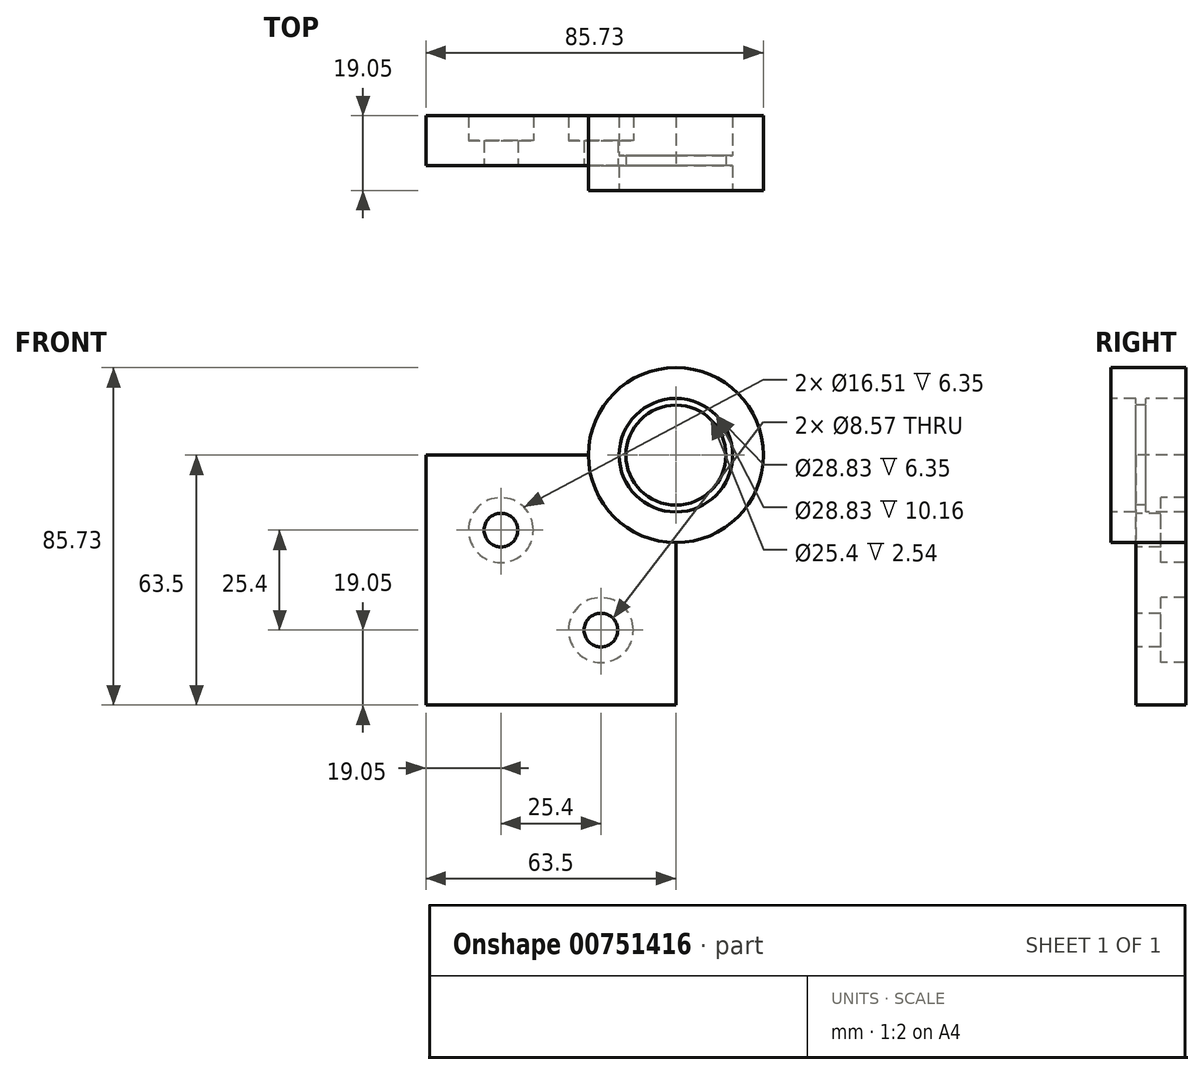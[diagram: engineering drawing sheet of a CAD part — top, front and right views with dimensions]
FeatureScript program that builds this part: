
annotation { "Feature Type Name" : "Feature", "Feature Type Description" : "" }
export const myFeature = defineFeature(function(context is Context, id is Id, definition is map)
    precondition{}
    {
        {
            var Q0;
            Q0=qCreatedBy(makeId("Front.planeOp"),FACE);
            var sketch = newSketch(context, id + "F0", { "sketchPlane" : qUnion([Q0])});
            skCircle(sketch, "E0", {"center": v(0, 0) * mm, "radius": 14.41 * mm});
            skCircle(sketch, "E1", {"center": v(0, 0) * mm, "radius": 12.7 * mm});
            skCircle(sketch, "E2", {"center": v(0, 0) * mm, "radius": 22.23 * mm});
            skLineSegment(sketch, "E3.bottom", {"start": v(0, 0) * mm, "end": v(-63.5, 0) * mm});
            skLineSegment(sketch, "E3.top", {"start": v(0, -63.5) * mm, "end": v(-63.5, -63.5) * mm});
            skLineSegment(sketch, "E3.left", {"start": v(0, 0) * mm, "end": v(0, -63.5) * mm});
            skLineSegment(sketch, "E3.right", {"start": v(-63.5, 0) * mm, "end": v(-63.5, -63.5) * mm});
            skCircle(sketch, "E4", {"center": v(-44.45, -19.05) * mm, "radius": 4.29 * mm});
            skCircle(sketch, "E5", {"center": v(-19.05, -44.45) * mm, "radius": 4.29 * mm});
            skCircle(sketch, "E6", {"center": v(-44.45, -19.05) * mm, "radius": 8.26 * mm});
            skCircle(sketch, "E7", {"center": v(-19.05, -44.45) * mm, "radius": 8.26 * mm});
            skSolve(sketch);
        }
        {
            var Q0;
            {var subQ0=sQuery(id+"F0.wireOp",EDGE,"E3.top");Q0=makeQuery(id+"F0.imprint","IMPRINT",FACE,{"disambiguationData":[TD([[makeQuery(id+"F0.imprint","IMPRINT",EDGE,{"derivedFrom":subQ0}),-1.0]])]});}
            extrude(context, id + "F1", {"entities" : qUnion([Q0]), "depth" : 12.7 * mm, "offsetDistance" : 25.4 * mm});
        }
        {
            var Q0;
            Q0=makeQuery(id+"F0.imprint","IMPRINT",FACE,{"disambiguationData":[TD([[makeQuery(id+"F0.imprint","IMPRINT",EDGE,{"derivedFrom":sQuery(id+"F0.wireOp",EDGE,"E4")}),-1.0]])]});
            var Q1;
            Q1=makeQuery(id+"F0.imprint","IMPRINT",FACE,{"disambiguationData":[TD([[makeQuery(id+"F0.imprint","IMPRINT",EDGE,{"derivedFrom":sQuery(id+"F0.wireOp",EDGE,"E5")}),-1.0]])]});
            extrude(context, id + "F2", {"entities" : qUnion([Q0, Q1]), "operationType" : NewBodyOperationType.ADD, "depth" : 6.35 * mm, "offsetDistance" : 25.4 * mm});
        }
        {
            var Q0;
            {var subQ0=sQuery(id+"F0.wireOp",EDGE,"E3.bottom");var subQ1=sQuery(id+"F0.wireOp",EDGE,"E0");var subQ2=makeQuery(id+"F0.imprint","INTERSECT",VERTEX,{"derivedFrom":[subQ1,subQ0]});Q0=makeQuery(id+"F0.imprint","IMPRINT",FACE,{"disambiguationData":[TD([[makeQuery(id+"F0.imprint","IMPRINT",EDGE,{"disambiguationData":[TD([[subQ2,-1.0]])],"derivedFrom":subQ1}),-1.0]])]});}
            var Q1;
            {var subQ0=sQuery(id+"F0.wireOp",EDGE,"E3.bottom");var subQ1=sQuery(id+"F0.wireOp",EDGE,"E0");var subQ2=makeQuery(id+"F0.imprint","INTERSECT",VERTEX,{"derivedFrom":[subQ1,subQ0]});Q1=makeQuery(id+"F0.imprint","IMPRINT",FACE,{"disambiguationData":[TD([[makeQuery(id+"F0.imprint","IMPRINT",EDGE,{"disambiguationData":[TD([[subQ2,1.0]])],"derivedFrom":subQ1}),-1.0]])]});}
            extrude(context, id + "F3", {"entities" : qUnion([Q0, Q1]), "operationType" : NewBodyOperationType.ADD, "depth" : 12.7 * mm, "offsetDistance" : 25.4 * mm, "hasSecondDirection" : true, "secondDirectionOppositeDirection" : true, "secondDirectionDepth" : 6.35 * mm});
        }
        {
            var Q0;
            {var subQ0=sQuery(id+"F0.wireOp",EDGE,"E3.bottom");var subQ1=sQuery(id+"F0.wireOp",EDGE,"E0");var subQ2=makeQuery(id+"F0.imprint","INTERSECT",VERTEX,{"derivedFrom":[subQ1,subQ0]});Q0=makeQuery(id+"F0.imprint","IMPRINT",FACE,{"disambiguationData":[TD([[makeQuery(id+"F0.imprint","IMPRINT",EDGE,{"disambiguationData":[TD([[subQ2,-1.0]])],"derivedFrom":subQ1}),1.0]])]});}
            var Q1;
            {var subQ0=sQuery(id+"F0.wireOp",EDGE,"E3.bottom");var subQ1=sQuery(id+"F0.wireOp",EDGE,"E0");var subQ2=makeQuery(id+"F0.imprint","INTERSECT",VERTEX,{"derivedFrom":[subQ1,subQ0]});Q1=makeQuery(id+"F0.imprint","IMPRINT",FACE,{"disambiguationData":[TD([[makeQuery(id+"F0.imprint","IMPRINT",EDGE,{"disambiguationData":[TD([[subQ2,1.0]])],"derivedFrom":subQ1}),1.0]])]});}
            extrude(context, id + "F4", {"entities" : qUnion([Q0, Q1]), "operationType" : NewBodyOperationType.ADD, "depth" : 2.54 * mm, "offsetDistance" : 25.4 * mm});
        }
        {
            var Q0;
            Q0=makeQuery(id+"F1.opExtrude","SWEPT_BODY",BODY,{"disambiguationData":[OSD([sQuery(id+"F0.wireOp",EDGE,"E2"),sQuery(id+"F0.wireOp",EDGE,"E3.bottom"),sQuery(id+"F0.wireOp",EDGE,"E3.top"),sQuery(id+"F0.wireOp",EDGE,"E3.left"),sQuery(id+"F0.wireOp",EDGE,"E3.right"),sQuery(id+"F0.wireOp",EDGE,"E6"),sQuery(id+"F0.wireOp",EDGE,"E7")])]});
            var Q1;
            Q1=qCreatedBy(makeId("Front.planeOp"),FACE);
            mirror(context, id + "F5", {"entities" : qUnion([Q0]), "mirrorPlane" : qUnion([Q1])});
        }
        {
            var Q0;
            Q0=makeQuery(id+"F1.opExtrude","SWEPT_BODY",BODY,{"disambiguationData":[OSD([sQuery(id+"F0.wireOp",EDGE,"E2"),sQuery(id+"F0.wireOp",EDGE,"E3.bottom"),sQuery(id+"F0.wireOp",EDGE,"E3.top"),sQuery(id+"F0.wireOp",EDGE,"E3.left"),sQuery(id+"F0.wireOp",EDGE,"E3.right"),sQuery(id+"F0.wireOp",EDGE,"E6"),sQuery(id+"F0.wireOp",EDGE,"E7")])]});
            deleteBodies(context, id + "F6", {"entities" : qUnion([Q0])});
        }
    });
